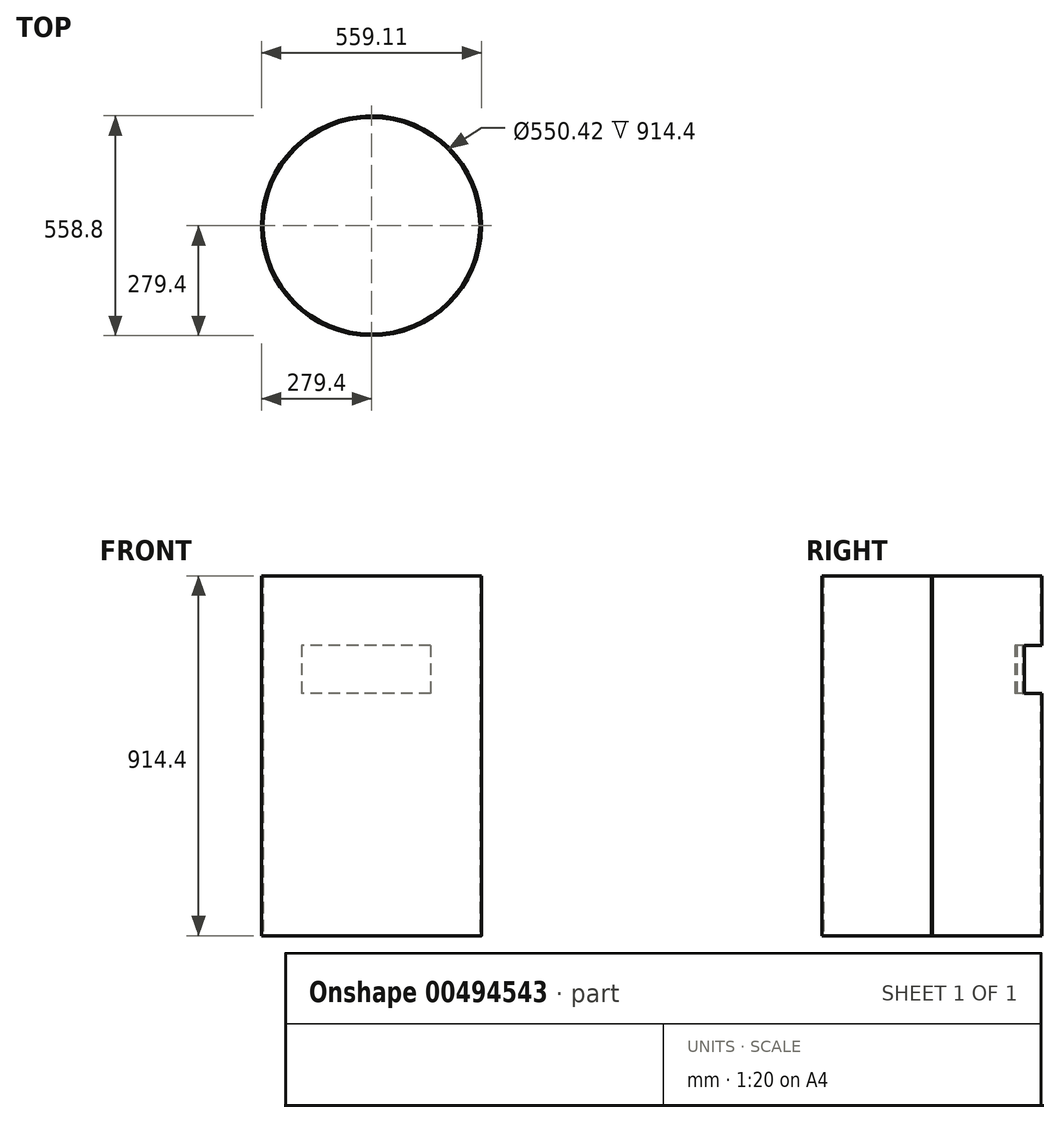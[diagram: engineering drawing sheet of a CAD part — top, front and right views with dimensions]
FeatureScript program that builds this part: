
annotation { "Feature Type Name" : "Feature", "Feature Type Description" : "" }
export const myFeature = defineFeature(function(context is Context, id is Id, definition is map)
    precondition{}
    {
        {
            var Q0;
            Q0=qCreatedBy(makeId("Top.planeOp"),FACE);
            var sketch = newSketch(context, id + "F0", { "sketchPlane" : qUnion([Q0])});
            skCircle(sketch, "E0", {"center": v(0, 0) * mm, "radius": 279.4 * mm});
            skCircle(sketch, "E1", {"center": v(0, 0) * mm, "radius": 275.2 * mm});
            skSolve(sketch);
        }
        {
            var Q0;
            Q0=qSketchRegion(id+"F0",true);
            extrude(context, id + "F1", {"entities" : qUnion([Q0]), "depth" : 914.4 * mm, "offsetDistance" : 25.4 * mm});
        }
        {
            var Q0;
            Q0=qCreatedBy(makeId("Front.planeOp"),FACE);
            var sketch = newSketch(context, id + "F2", { "sketchPlane" : qUnion([Q0])});
            skLineSegment(sketch, "E2.bottom", {"start": v(150.52, 738.1) * mm, "end": v(-177.13, 738.1) * mm});
            skLineSegment(sketch, "E2.top", {"start": v(150.52, 615.07) * mm, "end": v(-177.13, 615.07) * mm});
            skLineSegment(sketch, "E2.left", {"start": v(150.52, 738.1) * mm, "end": v(150.52, 615.07) * mm});
            skLineSegment(sketch, "E2.right", {"start": v(-177.13, 738.1) * mm, "end": v(-177.13, 615.07) * mm});
            skSolve(sketch);
        }
        {
            var Q0;
            Q0=makeQuery(id+"F2.imprint","IMPRINT",FACE,{"disambiguationData":[TD([[makeQuery(id+"F2.imprint","IMPRINT",EDGE,{"derivedFrom":sQuery(id+"F2.wireOp",EDGE,"E2.bottom")}),1.0]])]});
            var Q1;
            Q1=sQuery(id+"F2.wireOp",EDGE,"E2.right");
            var Q2;
            Q2=sQuery(id+"F2.wireOp",EDGE,"E2.bottom");
            var Q3;
            Q3=sQuery(id+"F2.wireOp",EDGE,"E2.left");
            var Q4;
            Q4=sQuery(id+"F2.wireOp",EDGE,"E2.top");
            extrude(context, id + "F3", {"entities" : qUnion([Q0]), "operationType" : NewBodyOperationType.REMOVE, "surfaceEntities" : qUnion([Q1, Q2, Q3, Q4]), "endBound" : BoundingType.THROUGH_ALL, "oppositeDirection" : true, "depth" : 449.58 * mm});
        }
        {
            var Q0;
            Q0=qCreatedBy(makeId("Top.planeOp"),FACE);
            var sketch = newSketch(context, id + "F4", { "sketchPlane" : qUnion([Q0])});
            skCircle(sketch, "E3", {"center": v(277.64, 0) * mm, "radius": 2.07 * mm});
            skSolve(sketch);
        }
        {
            var Q0;
            Q0 = qSketchRegion(id + "F4", true);
            extrude(context, id + "F5", {"entities" : qUnion([Q0]), "operationType" : NewBodyOperationType.ADD, "depth" : 914.4 * mm, "offsetDistance" : 25.4 * mm});
        }
    });
